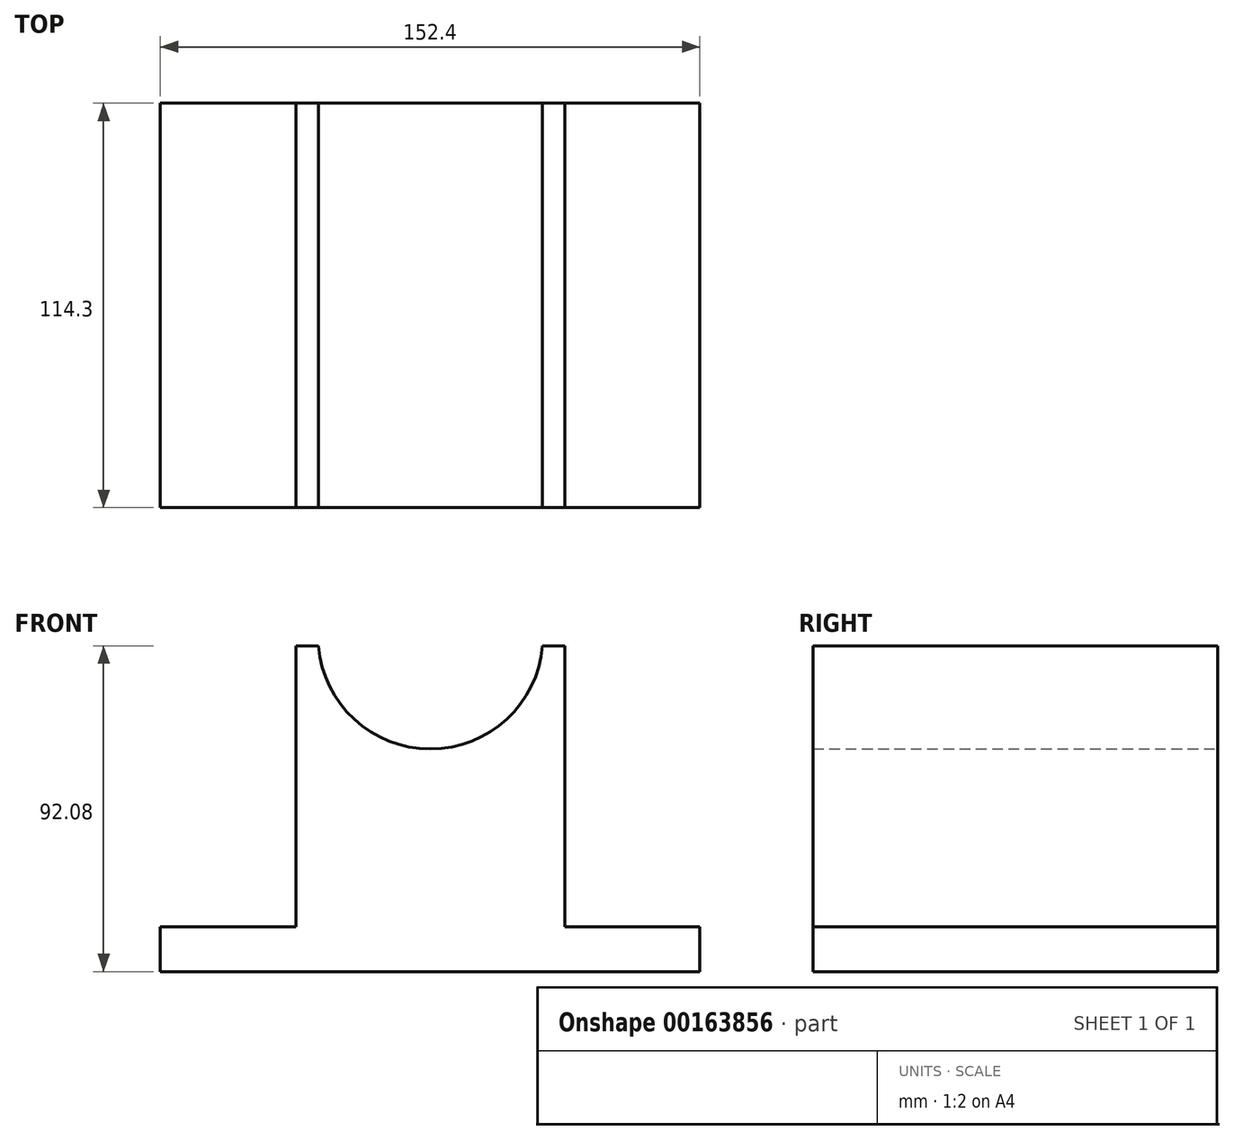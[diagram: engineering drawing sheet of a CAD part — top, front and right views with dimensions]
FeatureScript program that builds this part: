
annotation { "Feature Type Name" : "Feature", "Feature Type Description" : "" }
export const myFeature = defineFeature(function(context is Context, id is Id, definition is map)
    precondition{}
    {
        {
            var Q0;
            Q0=qCreatedBy(makeId("Front.planeOp"),FACE);
            var sketch = newSketch(context, id + "F0", { "sketchPlane" : qUnion([Q0])});
            skLineSegment(sketch, "E0", {"start": v(0, 0) * mm, "end": v(152.4, 0) * mm});
            skLineSegment(sketch, "E1", {"start": v(152.4, 0) * mm, "end": v(152.4, 12.7) * mm});
            skLineSegment(sketch, "E2", {"start": v(152.4, 12.7) * mm, "end": v(114.3, 12.7) * mm});
            skLineSegment(sketch, "E3", {"start": v(114.3, 12.7) * mm, "end": v(114.3, 92.08) * mm});
            skLineSegment(sketch, "E4", {"start": v(38.3, 92.08) * mm, "end": v(38.3, 12.7) * mm});
            skLineSegment(sketch, "E5", {"start": v(38.3, 12.7) * mm, "end": v(0, 12.7) * mm});
            skLineSegment(sketch, "E6", {"start": v(0, 12.7) * mm, "end": v(0, 0) * mm});
            skLineSegment(sketch, "E7", {"start": v(38.3, 92.08) * mm, "end": v(44.66, 92.08) * mm});
            skLineSegment(sketch, "E8", {"start": v(114.3, 92.08) * mm, "end": v(107.95, 92.08) * mm});
            skArc(sketch, "E9", {"start": v(44.66, 92.08) * mm, "mid": v(76.3, 62.88) * mm, "end": v(107.95, 92.08) * mm});
            skSolve(sketch);
        }
        {
            var Q0;
            Q0=makeQuery(id+"F0.imprint","IMPRINT",FACE,{"disambiguationData":[TD([[makeQuery(id+"F0.imprint","IMPRINT",EDGE,{"derivedFrom":sQuery(id+"F0.wireOp",EDGE,"E0")}),1.0]])]});
            extrude(context, id + "F1", {"entities" : qUnion([Q0]), "depth" : 114.3 * mm});
        }
    });
